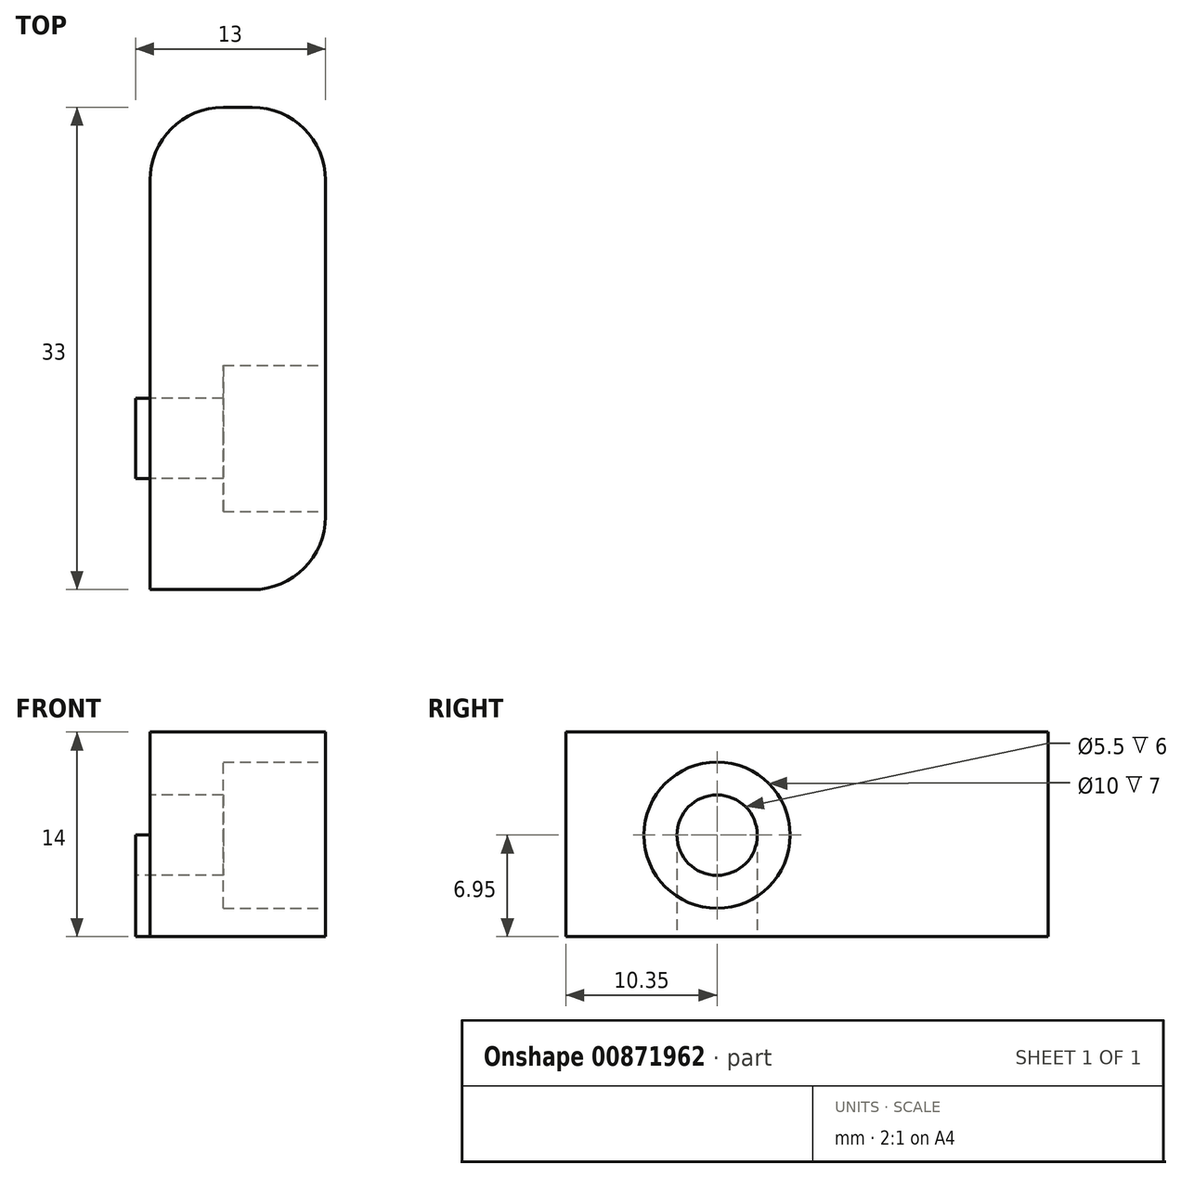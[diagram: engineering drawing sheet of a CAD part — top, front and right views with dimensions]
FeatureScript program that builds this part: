
annotation { "Feature Type Name" : "Feature", "Feature Type Description" : "" }
export const myFeature = defineFeature(function(context is Context, id is Id, definition is map)
    precondition{}
    {
        {
            var Q0;
            Q0=qCreatedBy(makeId("Top.planeOp"),FACE);
            var sketch = newSketch(context, id + "F0", { "sketchPlane" : qUnion([Q0])});
            skLineSegment(sketch, "E0.bottom", {"start": v(6, 16.5) * mm, "end": v(-6, 16.5) * mm});
            skLineSegment(sketch, "E0.top", {"start": v(6, -16.5) * mm, "end": v(-6, -16.5) * mm});
            skLineSegment(sketch, "E0.left", {"start": v(6, 16.5) * mm, "end": v(6, -16.5) * mm});
            skLineSegment(sketch, "E0.right", {"start": v(-6, 16.5) * mm, "end": v(-6, -16.5) * mm});
            skPoint(sketch, "E0.middle", {"position": v(0, 0) * mm});
            skLineSegment(sketch, "E1.bottom", {"start": v(-6, 16.5) * mm, "end": v(6, 16.5) * mm});
            skLineSegment(sketch, "E1.top", {"start": v(-6, 28.5) * mm, "end": v(6, 28.5) * mm});
            skLineSegment(sketch, "E1.left", {"start": v(-6, 16.5) * mm, "end": v(-6, 28.5) * mm});
            skLineSegment(sketch, "E1.right", {"start": v(6, 16.5) * mm, "end": v(6, 28.5) * mm});
            skCircle(sketch, "E2", {"center": v(0, 22.5) * mm, "radius": 2.15 * mm});
            skPoint(sketch, "E2.centerSnap0", {"position": v(-6, 22.5) * mm});
            skPoint(sketch, "E2.centerSnap1", {"position": v(0, 16.5) * mm});
            skSolve(sketch);
        }
        {
            var Q0;
            Q0=makeQuery(id+"F0.imprint","IMPRINT",FACE,{"disambiguationData":[TD([[makeQuery(id+"F0.imprint","IMPRINT",EDGE,{"derivedFrom":sQuery(id+"F0.wireOp",EDGE,"E0.top")}),-1.0]])]});
            var Q1;
            Q1=makeQuery(id+"F0.imprint","IMPRINT",FACE,{"disambiguationData":[TD([[makeQuery(id+"F0.imprint","IMPRINT",EDGE,{"derivedFrom":sQuery(id+"F0.wireOp",EDGE,"E1.bottom")}),1.0]])]});
            extrude(context, id + "F1", {"entities" : qUnion([Q0, Q1]), "depth" : 14 * mm, "offsetDistance" : 25 * mm});
        }
        {
            var Q0;
            Q0=makeQuery(id+"F1.opExtrude","SWEPT_FACE",FACE,{"disambiguationData":[OSD([sQuery(id+"F0.wireOp",EDGE,"E0.right"),sQuery(id+"F0.wireOp",EDGE,"E1.left")])]});
            var sketch = newSketch(context, id + "F2", { "sketchPlane" : qUnion([Q0])});
            skCircle(sketch, "E3", {"center": v(6.15, 6.95) * mm, "radius": 2.75 * mm});
            skLineSegment(sketch, "E4.bottom", {"start": v(3.4, 6.95) * mm, "end": v(8.9, 6.95) * mm});
            skLineSegment(sketch, "E4.top", {"start": v(3.4, 0) * mm, "end": v(8.9, 0) * mm});
            skLineSegment(sketch, "E4.left", {"start": v(3.4, 6.95) * mm, "end": v(3.4, 0) * mm});
            skLineSegment(sketch, "E4.right", {"start": v(8.9, 6.95) * mm, "end": v(8.9, 0) * mm});
            skSolve(sketch);
        }
        {
            var Q0;
            {var subQ0=sQuery(id+"F2.wireOp",EDGE,"E4.bottom");Q0=makeQuery(id+"F2.imprint","IMPRINT",FACE,{"disambiguationData":[TD([[makeQuery(id+"F2.imprint","IMPRINT",EDGE,{"derivedFrom":subQ0}),1.0]])]});}
            var Q1;
            {var subQ0=sQuery(id+"F2.wireOp",EDGE,"E4.bottom");Q1=makeQuery(id+"F2.imprint","IMPRINT",FACE,{"disambiguationData":[TD([[makeQuery(id+"F2.imprint","IMPRINT",EDGE,{"derivedFrom":subQ0}),-1.0]])]});}
            extrude(context, id + "F3", {"entities" : qUnion([Q0, Q1]), "operationType" : NewBodyOperationType.REMOVE, "oppositeDirection" : true, "depth" : 25 * mm, "offsetDistance" : 25 * mm});
        }
        {
            var Q0;
            Q0=makeQuery(id+"F2.imprint","IMPRINT",FACE,{"disambiguationData":[TD([[makeQuery(id+"F2.imprint","IMPRINT",EDGE,{"derivedFrom":sQuery(id+"F2.wireOp",EDGE,"E4.top")}),1.0]])]});
            extrude(context, id + "F4", {"entities" : qUnion([Q0]), "operationType" : NewBodyOperationType.ADD, "depth" : 1 * mm, "offsetDistance" : 25 * mm});
        }
        {
            var Q0;
            Q0=makeQuery(id+"F1.opExtrude","SWEPT_FACE",FACE,{"disambiguationData":[OSD([sQuery(id+"F0.wireOp",EDGE,"E0.left"),sQuery(id+"F0.wireOp",EDGE,"E1.right")])]});
            var sketch = newSketch(context, id + "F5", { "sketchPlane" : qUnion([Q0])});
            skCircle(sketch, "E5", {"center": v(-6.15, 6.95) * mm, "radius": 5 * mm});
            skSolve(sketch);
        }
        {
            var Q0;
            Q0=makeQuery(id+"F5.imprint","IMPRINT",FACE,{"disambiguationData":[TD([[makeQuery(id+"F5.imprint","IMPRINT",EDGE,{"derivedFrom":sQuery(id+"F5.wireOp",EDGE,"E5")}),1.0]])]});
            extrude(context, id + "F6", {"entities" : qUnion([Q0]), "operationType" : NewBodyOperationType.REMOVE, "oppositeDirection" : true, "depth" : 7 * mm, "offsetDistance" : 25 * mm});
        }
        {
            var Q0;
            Q0=makeQuery(id+"F1.opExtrude","SWEPT_EDGE",EDGE,{"disambiguationData":[OSD([sQuery(id+"F0.wireOp",EDGE,"E1.top"),sQuery(id+"F0.wireOp",EDGE,"E1.right")])]});
            var Q1;
            Q1=makeQuery(id+"F1.opExtrude","SWEPT_EDGE",EDGE,{"disambiguationData":[OSD([sQuery(id+"F0.wireOp",EDGE,"E1.top"),sQuery(id+"F0.wireOp",EDGE,"E1.left")])]});
            var Q2;
            Q2=makeQuery(id+"F1.opExtrude","SWEPT_EDGE",EDGE,{"disambiguationData":[OSD([sQuery(id+"F0.wireOp",EDGE,"E0.top"),sQuery(id+"F0.wireOp",EDGE,"E0.left")])]});
            fillet(context, id + "F7", {"entities" : qUnion([Q0, Q1, Q2]), "radius" : 5 * mm, "tangentPropagation" : true, "allowEdgeOverflow" : false});
        }
    });
